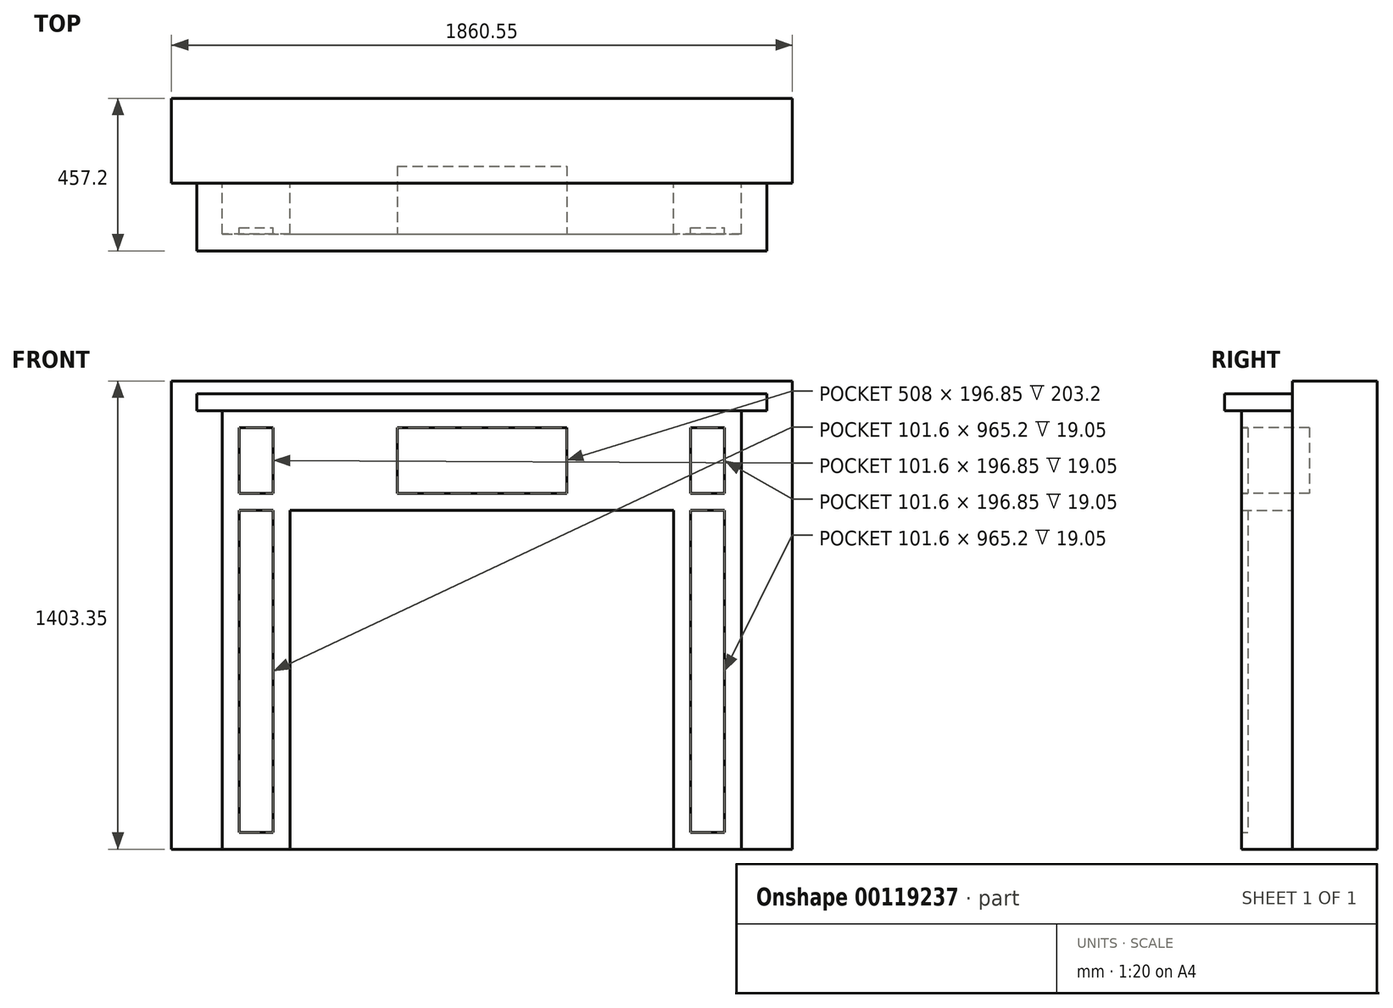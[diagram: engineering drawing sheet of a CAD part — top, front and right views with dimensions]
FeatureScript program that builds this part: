
annotation { "Feature Type Name" : "Feature", "Feature Type Description" : "" }
export const myFeature = defineFeature(function(context is Context, id is Id, definition is map)
    precondition{}
    {
        {
            var Q0;
            Q0=qCreatedBy(makeId("Front.planeOp"),FACE);
            var sketch = newSketch(context, id + "F0", { "sketchPlane" : qUnion([Q0])});
            skLineSegment(sketch, "E0", {"start": v(0, 0) * mm, "end": v(0, 1403.35) * mm});
            skLineSegment(sketch, "E1", {"start": v(0, 1403.35) * mm, "end": v(1860.55, 1403.35) * mm});
            skLineSegment(sketch, "E2", {"start": v(1860.55, 1403.35) * mm, "end": v(1860.55, 0) * mm});
            skLineSegment(sketch, "E3", {"start": v(1860.55, 0) * mm, "end": v(0, 0) * mm});
            skSolve(sketch);
        }
        {
            var Q0;
            Q0=qCreatedBy(makeId("Front.planeOp"),FACE);
            var sketch = newSketch(context, id + "F1", { "sketchPlane" : qUnion([Q0])});
            skLineSegment(sketch, "E4.bottom", {"start": v(463.55, 927.1) * mm, "end": v(1397, 927.1) * mm});
            skLineSegment(sketch, "E4.top", {"start": v(463.55, 228.6) * mm, "end": v(1397, 228.6) * mm});
            skLineSegment(sketch, "E4.left", {"start": v(463.55, 927.1) * mm, "end": v(463.55, 228.6) * mm});
            skLineSegment(sketch, "E4.right", {"start": v(1397, 927.1) * mm, "end": v(1397, 228.6) * mm});
            skLineSegment(sketch, "E5", {"start": v(930.27, 1401.22) * mm, "end": v(930.28, 0) * mm, "construction": true});
            skLineSegment(sketch, "E6.bottom", {"start": v(676.27, 1365.25) * mm, "end": v(1184.27, 1365.25) * mm});
            skLineSegment(sketch, "E6.top", {"start": v(676.27, 1168.4) * mm, "end": v(1184.27, 1168.4) * mm});
            skLineSegment(sketch, "E6.left", {"start": v(676.27, 1365.25) * mm, "end": v(676.27, 1168.4) * mm});
            skLineSegment(sketch, "E6.right", {"start": v(1184.27, 1365.25) * mm, "end": v(1184.27, 1168.4) * mm});
            skSolve(sketch);
        }
        {
            var Q0;
            Q0=makeQuery(id+"F0.imprint","IMPRINT",FACE,{"disambiguationData":[TD([[makeQuery(id+"F0.imprint","IMPRINT",EDGE,{"derivedFrom":sQuery(id+"F0.wireOp",EDGE,"E0")}),-1.0]])]});
            extrude(context, id + "F2", {"entities" : qUnion([Q0]), "oppositeDirection" : true, "depth" : 254 * mm});
        }
        {
            var Q0;
            Q0=makeQuery(id+"F2.opExtrude","CAP_FACE",FACE,{"disambiguationData":[OSD([sQuery(id+"F0.wireOp",EDGE,"E0"),sQuery(id+"F0.wireOp",EDGE,"E1"),sQuery(id+"F0.wireOp",EDGE,"E2"),sQuery(id+"F0.wireOp",EDGE,"E3")])],"isStart":true});
            var sketch = newSketch(context, id + "F3", { "sketchPlane" : qUnion([Q0])});
            skLineSegment(sketch, "E7.bottom", {"start": v(76.2, 1365.25) * mm, "end": v(1784.35, 1365.25) * mm});
            skLineSegment(sketch, "E7.top", {"start": v(76.2, 1314.45) * mm, "end": v(1784.35, 1314.45) * mm});
            skLineSegment(sketch, "E7.left", {"start": v(76.2, 1365.25) * mm, "end": v(76.2, 1314.45) * mm});
            skLineSegment(sketch, "E7.right", {"start": v(1784.35, 1365.25) * mm, "end": v(1784.35, 1314.45) * mm});
            skSolve(sketch);
        }
        {
            var Q0;
            Q0=makeQuery(id+"F3.imprint","IMPRINT",FACE,{"disambiguationData":[TD([[makeQuery(id+"F3.imprint","IMPRINT",EDGE,{"derivedFrom":sQuery(id+"F3.wireOp",EDGE,"E7.bottom")}),-1.0]])]});
            extrude(context, id + "F4", {"entities" : qUnion([Q0]), "operationType" : NewBodyOperationType.ADD, "depth" : 203.2 * mm});
        }
        {
            var Q0;
            Q0=makeQuery(id+"F3.imprint","IMPRINT",FACE,{"disambiguationData":[TD([[makeQuery(id+"F3.imprint","IMPRINT",EDGE,{"derivedFrom":sQuery(id+"F3.wireOp",EDGE,"E7.bottom")}),1.0]])]});
            var sketch = newSketch(context, id + "F5", { "sketchPlane" : qUnion([Q0])});
            skLineSegment(sketch, "E8.top", {"start": v(152.4, 0) * mm, "end": v(355.6, 0) * mm});
            skLineSegment(sketch, "E8.left", {"start": v(152.4, 1314.45) * mm, "end": v(152.4, 0) * mm});
            skLineSegment(sketch, "E8.right", {"start": v(355.6, 1016) * mm, "end": v(355.6, 0) * mm});
            skLineSegment(sketch, "E9.top", {"start": v(1504.95, 0) * mm, "end": v(1708.15, 0) * mm});
            skLineSegment(sketch, "E9.left", {"start": v(1504.95, 1016) * mm, "end": v(1504.95, 0) * mm});
            skLineSegment(sketch, "E9.right", {"start": v(1708.15, 1314.45) * mm, "end": v(1708.15, 0) * mm});
            skLineSegment(sketch, "E10.bottom", {"start": v(203.2, 50.8) * mm, "end": v(304.8, 50.8) * mm});
            skLineSegment(sketch, "E10.top", {"start": v(203.2, 1016) * mm, "end": v(304.8, 1016) * mm});
            skLineSegment(sketch, "E10.left", {"start": v(203.2, 50.8) * mm, "end": v(203.2, 1016) * mm});
            skLineSegment(sketch, "E10.right", {"start": v(304.8, 50.8) * mm, "end": v(304.8, 1016) * mm});
            skPoint(sketch, "E11.oppositeSnap0", {"position": v(254, 50.8) * mm});
            skLineSegment(sketch, "E11.bottom", {"start": v(1555.75, 1016) * mm, "end": v(1657.35, 1016) * mm});
            skLineSegment(sketch, "E11.top", {"start": v(1555.75, 50.8) * mm, "end": v(1657.35, 50.8) * mm});
            skLineSegment(sketch, "E11.left", {"start": v(1555.75, 1016) * mm, "end": v(1555.75, 50.8) * mm});
            skLineSegment(sketch, "E11.right", {"start": v(1657.35, 1016) * mm, "end": v(1657.35, 50.8) * mm});
            skLineSegment(sketch, "E12", {"start": v(355.6, 1016) * mm, "end": v(1504.95, 1016) * mm});
            skLineSegment(sketch, "E13.bottom", {"start": v(203.2, 1066.8) * mm, "end": v(304.8, 1066.8) * mm});
            skLineSegment(sketch, "E13.top", {"start": v(203.2, 1263.65) * mm, "end": v(304.8, 1263.65) * mm});
            skLineSegment(sketch, "E13.left", {"start": v(203.2, 1066.8) * mm, "end": v(203.2, 1263.65) * mm});
            skLineSegment(sketch, "E13.right", {"start": v(304.8, 1066.8) * mm, "end": v(304.8, 1263.65) * mm});
            skLineSegment(sketch, "E14.bottom", {"start": v(1555.75, 1066.8) * mm, "end": v(1657.35, 1066.8) * mm});
            skLineSegment(sketch, "E14.top", {"start": v(1555.75, 1263.65) * mm, "end": v(1657.35, 1263.65) * mm});
            skLineSegment(sketch, "E14.left", {"start": v(1555.75, 1066.8) * mm, "end": v(1555.75, 1263.65) * mm});
            skLineSegment(sketch, "E14.right", {"start": v(1657.35, 1066.8) * mm, "end": v(1657.35, 1263.65) * mm});
            skPoint(sketch, "E8.bottom.end.orphan", {"position": v(355.6, 1314.45) * mm});
            skPoint(sketch, "E9.bottom.start.orphan", {"position": v(1504.95, 1314.45) * mm});
            skLineSegment(sketch, "E15", {"start": v(152.4, 1314.45) * mm, "end": v(1708.15, 1314.45) * mm});
            skSolve(sketch);
        }
        {
            var Q0;
            Q0 = qSketchRegion(id + "F5", true);
            extrude(context, id + "F6", {"entities" : qUnion([Q0]), "operationType" : NewBodyOperationType.ADD, "depth" : 152.4 * mm});
        }
        {
            var Q0;
            Q0=makeQuery(id+"F6.opExtrude","CAP_FACE",FACE,{"disambiguationData":[OSD([sQuery(id+"F5.wireOp",EDGE,"E8.top"),sQuery(id+"F5.wireOp",EDGE,"E8.left"),sQuery(id+"F5.wireOp",EDGE,"E8.right"),sQuery(id+"F5.wireOp",EDGE,"E9.top"),sQuery(id+"F5.wireOp",EDGE,"E9.left"),sQuery(id+"F5.wireOp",EDGE,"E9.right"),sQuery(id+"F5.wireOp",EDGE,"E10.bottom"),sQuery(id+"F5.wireOp",EDGE,"E10.top"),sQuery(id+"F5.wireOp",EDGE,"E10.left"),sQuery(id+"F5.wireOp",EDGE,"E10.right"),sQuery(id+"F5.wireOp",EDGE,"E11.bottom"),sQuery(id+"F5.wireOp",EDGE,"E11.top"),sQuery(id+"F5.wireOp",EDGE,"E11.left"),sQuery(id+"F5.wireOp",EDGE,"E11.right"),sQuery(id+"F5.wireOp",EDGE,"E12"),sQuery(id+"F5.wireOp",EDGE,"E13.bottom"),sQuery(id+"F5.wireOp",EDGE,"E13.top"),sQuery(id+"F5.wireOp",EDGE,"E13.left"),sQuery(id+"F5.wireOp",EDGE,"E13.right"),sQuery(id+"F5.wireOp",EDGE,"E14.bottom"),sQuery(id+"F5.wireOp",EDGE,"E14.top"),sQuery(id+"F5.wireOp",EDGE,"E14.left"),sQuery(id+"F5.wireOp",EDGE,"E14.right"),sQuery(id+"F5.wireOp",EDGE,"E15")])],"isStart":false});
            var sketch = newSketch(context, id + "F7", { "sketchPlane" : qUnion([Q0])});
            skLineSegment(sketch, "E16.bottom", {"start": v(676.27, 1263.65) * mm, "end": v(1184.27, 1263.65) * mm});
            skLineSegment(sketch, "E16.top", {"start": v(676.27, 1066.8) * mm, "end": v(1184.27, 1066.8) * mm});
            skLineSegment(sketch, "E16.left", {"start": v(676.27, 1263.65) * mm, "end": v(676.27, 1066.8) * mm});
            skLineSegment(sketch, "E16.right", {"start": v(1184.27, 1263.65) * mm, "end": v(1184.27, 1066.8) * mm});
            skSolve(sketch);
        }
        {
            var Q0;
            Q0=makeQuery(id+"F7.imprint","IMPRINT",FACE,{"disambiguationData":[TD([[makeQuery(id+"F7.imprint","IMPRINT",EDGE,{"derivedFrom":sQuery(id+"F7.wireOp",EDGE,"E16.bottom")}),-1.0]])]});
            extrude(context, id + "F8", {"entities" : qUnion([Q0]), "operationType" : NewBodyOperationType.REMOVE, "oppositeDirection" : true, "depth" : 203.2 * mm});
        }
        {
            var Q0;
            Q0=makeQuery(id+"F3.imprint","IMPRINT",FACE,{"disambiguationData":[TD([[makeQuery(id+"F3.imprint","IMPRINT",EDGE,{"derivedFrom":sQuery(id+"F3.wireOp",EDGE,"E7.bottom")}),1.0]])]});
            var sketch = newSketch(context, id + "F9", { "sketchPlane" : qUnion([Q0])});
            skLineSegment(sketch, "E17.bottom", {"start": v(203.2, 1016) * mm, "end": v(304.8, 1016) * mm});
            skLineSegment(sketch, "E17.top", {"start": v(203.2, 50.8) * mm, "end": v(304.8, 50.8) * mm});
            skLineSegment(sketch, "E17.left", {"start": v(203.2, 1016) * mm, "end": v(203.2, 50.8) * mm});
            skLineSegment(sketch, "E17.right", {"start": v(304.8, 1016) * mm, "end": v(304.8, 50.8) * mm});
            skLineSegment(sketch, "E18.bottom", {"start": v(203.2, 1263.65) * mm, "end": v(304.8, 1263.65) * mm});
            skLineSegment(sketch, "E18.top", {"start": v(203.2, 1066.8) * mm, "end": v(304.8, 1066.8) * mm});
            skLineSegment(sketch, "E18.left", {"start": v(203.2, 1263.65) * mm, "end": v(203.2, 1066.8) * mm});
            skLineSegment(sketch, "E18.right", {"start": v(304.8, 1263.65) * mm, "end": v(304.8, 1066.8) * mm});
            skLineSegment(sketch, "E19.bottom", {"start": v(1555.75, 1263.65) * mm, "end": v(1657.35, 1263.65) * mm});
            skLineSegment(sketch, "E19.top", {"start": v(1555.75, 1066.8) * mm, "end": v(1657.35, 1066.8) * mm});
            skLineSegment(sketch, "E19.left", {"start": v(1555.75, 1263.65) * mm, "end": v(1555.75, 1066.8) * mm});
            skLineSegment(sketch, "E19.right", {"start": v(1657.35, 1263.65) * mm, "end": v(1657.35, 1066.8) * mm});
            skLineSegment(sketch, "E20.bottom", {"start": v(1555.75, 1016) * mm, "end": v(1657.35, 1016) * mm});
            skLineSegment(sketch, "E20.top", {"start": v(1555.75, 50.8) * mm, "end": v(1657.35, 50.8) * mm});
            skLineSegment(sketch, "E20.left", {"start": v(1555.75, 1016) * mm, "end": v(1555.75, 50.8) * mm});
            skLineSegment(sketch, "E20.right", {"start": v(1657.35, 1016) * mm, "end": v(1657.35, 50.8) * mm});
            skSolve(sketch);
        }
        {
            var Q0;
            Q0 = qSketchRegion(id + "F9", true);
            extrude(context, id + "F10", {"entities" : qUnion([Q0]), "operationType" : NewBodyOperationType.ADD, "depth" : 133.35 * mm});
        }
    });
